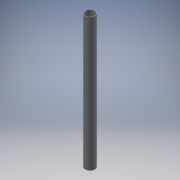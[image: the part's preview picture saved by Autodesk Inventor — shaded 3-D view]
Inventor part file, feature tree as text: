
AUTODESK INVENTOR PART (.ipt)
format: ipt  version: 2016 (Build 200138000, 138)  size: 91,648 bytes
history: native  units: in
note: dims shown in document units (in); Inventor stores cm internally (conversion verified against a paired STEP export)
features: extrude x2, sketch x2
ambient origin geometry x8: Origin, YZ Plane, XZ Plane, XY Plane, X Axis, Y Axis, Z Axis, Center Point
bodies: Solid1 (feature_tree)
feature tree (4):
  extrude  "Extrusion1"  Depth=8.625in TaperAngle=0.0deg
  extrude  "Extrusion2"  Depth=10.625in TaperAngle=0.0deg
  sketch  "Sketch1"  dims[d0=0.625in d1=8.625in d2=0.0in]
  sketch  "Sketch2"  dims[d3=0.564in d4=10.625in d5=0.0in]
